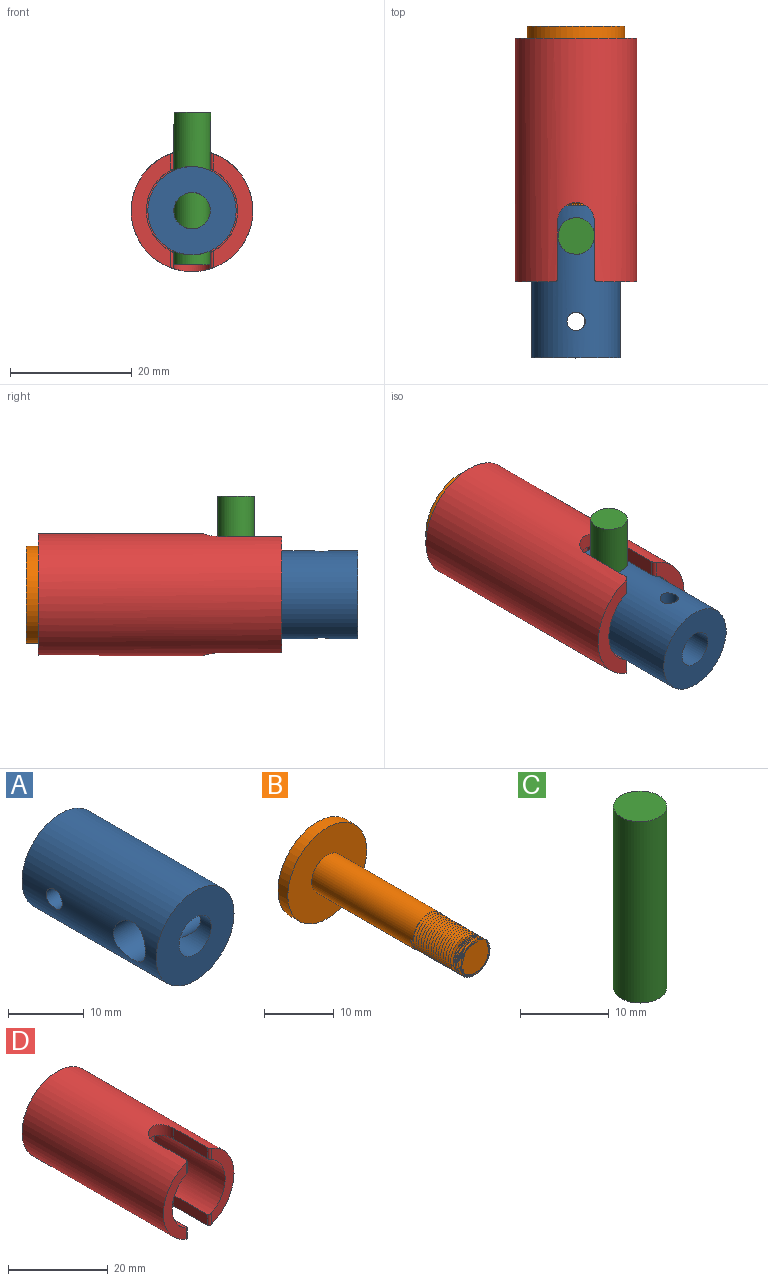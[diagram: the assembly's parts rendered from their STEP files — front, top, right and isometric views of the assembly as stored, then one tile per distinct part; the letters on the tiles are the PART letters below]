
ASSEMBLY  parts=4 mates=4
PART A: 9 faces, bbox 14.5x25x14.5 mm
  f0: cylinder r=3mm len=20mm, axis (0,1,0), area 326.3mm2, adj f4,f5,f6,f7,f8
  f1: cylinder r=3mm len=6mm, axis (0,1,0), area 58.2mm2, adj f3,f7,f8
  f2: cylinder r=7.25mm len=25mm, axis (0,1,0), area 1066.8mm2, adj f3,f4,f5,f6,f7,f8
  f3: plane 14.5x14.5mm, normal (0,-1,0), area 136.9mm2, adj f1,f2
  f4: plane 14.5x14.5mm, normal (0,1,0), area 136.9mm2, adj f0,f2
  f5: cylinder r=1.5mm len=4.65mm, axis (-1,0,0), area 41.2mm2, adj f0,f2
  f6: cylinder r=1.5mm len=4.65mm, axis (-1,0,0), area 41.2mm2, adj f0,f2
  f7: cylinder r=3mm len=7.25mm, axis (-1,0,0), area 94.6mm2, adj f0,f1,f2
  f8: cylinder r=3mm len=7.25mm, axis (-1,0,0), area 94.6mm2, adj f0,f1,f2
PART B: 9 faces, bbox 16.4x32.7x16.4 mm
  f0: cylinder r=3.17mm len=20.63mm, axis (0,-1,0), area 406.5mm2, adj f1,f6,f7
  f1: plane 16x16mm, normal (0,-1,0), area 169.4mm2, adj f0,f2
  f2: cylinder r=8mm len=16mm, axis (0,-1,0), area 100.5mm2, adj f1,f3
  f3: plane 16x16mm, normal (0,1,0), area 201.1mm2, adj f2
  f4: bspline ~9.92x7.18mm, area 172.3mm2, adj f5,f6,f8
  f5: bspline ~10.17x7.18mm, area 177mm2, adj f4,f6,f7,f8
  f6: plane 0.54x0.5mm, normal (0,0,-1), area 0.1mm2, adj f0,f4,f5,f7
  f7: bspline ~7.33x6.35mm, area 1.5mm2, adj f0,f5,f6
  f8: plane 6.17x6.17mm, normal (0,-1,0), area 26.3mm2, adj f4,f5
PART C: 3 faces, bbox 6x6x25 mm
  f0: cylinder r=3mm len=25mm, axis (0,0,-1), area 471.2mm2, adj f1,f2
  f1: plane 6x6mm, normal (0,0,1), area 28.3mm2, adj f0
  f2: plane 6x6mm, normal (0,0,-1), area 28.3mm2, adj f0
PART D: 17 faces, bbox 20x40x20 mm
  f0: plane 18.74x6.5mm, normal (0,-1,0), area 50.7mm2, adj f2,f4,f13,f15
  f1: plane 20x20mm, normal (0,1,0), area 285.9mm2, adj f2,f6
  f2: cylinder r=10mm len=40mm, axis (0,1,0), area 2362.6mm2, adj f0,f1,f3,f7,f8,f9,f10,f11
  f3: plane 18.74x6.5mm, normal (0,-1,0), area 50.7mm2, adj f2,f4,f14,f16
  f4: cylinder r=7.5mm len=20mm, axis (0,1,0), area 789.9mm2, adj f0,f3,f5,f7,f8,f9,f10,f11
  f5: plane 15x15mm, normal (0,-1,0), area 148.4mm2, adj f4,f6
  f6: cylinder r=3mm len=20mm, axis (0,1,0), area 377mm2, adj f1,f5
  f7: plane 9.5x2.67mm, normal (1,0,0), area 25.3mm2, adj f2,f4,f8,f14
  f8: cylinder r=3mm len=6mm, axis (0,0,1), area 24.3mm2, adj f2,f4,f7,f9
  f9: plane 9.5x2.67mm, normal (-1,0,0), area 25.3mm2, adj f2,f4,f8,f13
  f10: plane 9.5x2.67mm, normal (-1,0,0), area 25.3mm2, adj f2,f4,f11,f15
  f11: cylinder r=3mm len=6mm, axis (0,0,1), area 24.3mm2, adj f2,f4,f10,f12
  f12: plane 9.5x2.67mm, normal (1,0,0), area 25.3mm2, adj f2,f4,f11,f16
  f13: cylinder r=0.5mm len=2.91mm, axis (0,0,1), area 2.1mm2, adj f0,f2,f4,f9
  f14: cylinder r=0.5mm len=2.91mm, axis (0,0,-1), area 2.1mm2, adj f2,f3,f4,f7
  f15: cylinder r=0.5mm len=2.91mm, axis (0,0,1), area 2.1mm2, adj f0,f2,f4,f10
  f16: cylinder r=0.5mm len=2.91mm, axis (0,0,-1), area 2.1mm2, adj f2,f3,f4,f12
PLACE A rot(axis=(0.71,0,-0.71),180deg) t=(0,-54.5,0)mm
PLACE B at identity
PLACE C rot(axis=(0,0,1),143.8deg) t=(0.01,-34.5,3.63)mm
PLACE D t=(0,-2,0)mm
MATE planar D.f2 <-> B.f0  axis (0,1,0) through (0,-2,0)mm
MATE cylindrical D.f2 <-> B.f0  axis (0,1,0) through (0,-2,0)mm
MATE revolute C.f0 <-> A.f7  axis (0,0,-1) through (0.01,-34.5,3.63)mm
MATE revolute A.f0 <-> D.f2  axis (0,-1,0) through (0,-42,0)mm
